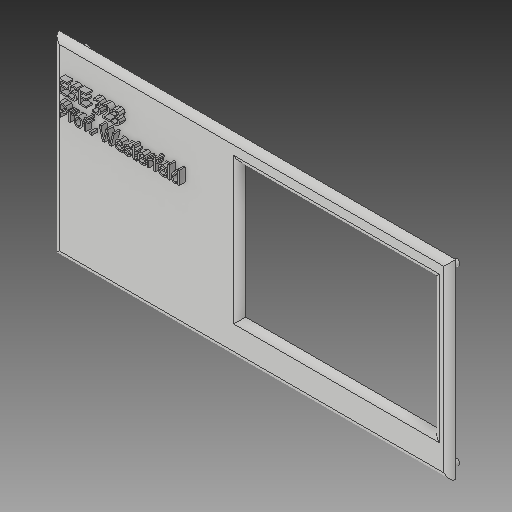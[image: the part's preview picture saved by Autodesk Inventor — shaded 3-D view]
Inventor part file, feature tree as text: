
AUTODESK INVENTOR PART (.ipt)
format: ipt  version: 2017 (Build 210142000, 142)  size: 671,232 bytes
history: native  units: in
note: dims shown in document units (in); Inventor stores cm internally (conversion verified against a paired STEP export)
features: extrude x5, sketch x5, fillet x1
ambient origin geometry x8: Origin, YZ Plane, XZ Plane, XY Plane, X Axis, Y Axis, Z Axis, Center Point
bodies: Solid1 (feature_tree)
feature tree (11):
  extrude  "Extrusion1"  Depth=2.5197in
  extrude  "Extrusion2"  Depth=0.0787in
  extrude  "Extrusion3"  Depth=1.1811in
  extrude  "Extrusion4"  Depth=0.1181in TaperAngle=0.0deg
  extrude  "Extrusion5"  Depth=0.0787in
  fillet  "Fillet1"  Radius=0.0787in
  sketch  "Sketch1"  dims[d0=5.2362in d1=2.5197in]
  sketch  "Sketch2"  dims[d2=0.0787in d3=0.0in d6=1.1811in]
  sketch  "Sketch3"  dims[d7=0.1181in d12=1.1811in]
  sketch  "Sketch4"  dims[d13=0.1378in d14=0.1181in d15=0.0in]
  sketch  "Sketch5"  dims[d19=0.0984in d22=0.0984in d25=0.0787in d29=0.0709in d30=0.1181in d31=0.0in d37=2.5591in d38=1.7717in d39=0.0787in d40=0.0in d41=0.0787in d42=0.0in d43=0.0787in]
